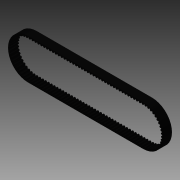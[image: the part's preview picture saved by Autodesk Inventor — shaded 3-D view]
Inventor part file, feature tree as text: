
AUTODESK INVENTOR PART (.ipt)
format: ipt  version: 2014 SP1 (Build 180222100, 222)  size: 1,027,584 bytes
history: native  units: mm
features: extrude x2, sketch x2, pattern_linear x1
ambient origin geometry x8: Origin, YZ Plane, XZ Plane, XY Plane, X Axis, Y Axis, Z Axis, Center Point
bodies: Solid1 (feature_tree)
feature tree (5):
  extrude  "Extrusion1"  Depth=15.0mm
  sketch  "Sketch2"  dims[d3=0.416667mm d4=1.5625mm d5=1.73mm d6=0.520833mm d7=0.100833mm d8=33.8201mm d10=197.651614mm d12=1220.0mm d15=607.801mm d16=65.532mm d19=15.0mm d20=0.0mm d22=0.25mm d23=1.73mm]
  pattern_linear  "Rectangular Pattern1"  Spacing1=1.5625mm  [1 undecoded]
  extrude  "Extrusion2"  Depth=1.73mm
  sketch  "Sketch1"  dims[d0=15.0mm d1=0.0mm d2=5.0mm]
note: 1 required parameter value undecoded (feature->parameter linkage not recoverable at this tier; creation-order binding heuristic only, values carry confidence <= 0.55)
